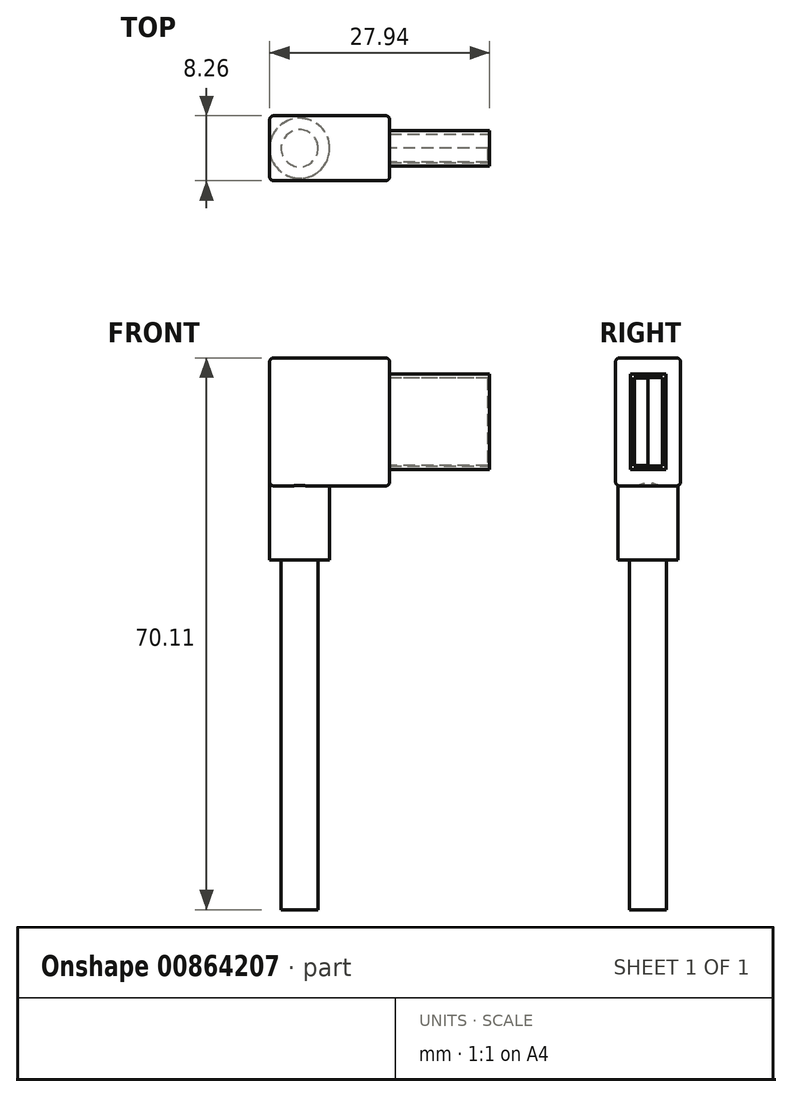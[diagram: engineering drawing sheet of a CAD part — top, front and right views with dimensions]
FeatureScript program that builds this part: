
annotation { "Feature Type Name" : "Feature", "Feature Type Description" : "" }
export const myFeature = defineFeature(function(context is Context, id is Id, definition is map)
    precondition{}
    {
        {
            var Q0;
            Q0=qCreatedBy(makeId("Front.planeOp"),FACE);
            var sketch = newSketch(context, id + "F0", { "sketchPlane" : qUnion([Q0])});
            skLineSegment(sketch, "E0.bottom", {"start": v(6.35, -6.08) * mm, "end": v(-6.35, -6.08) * mm});
            skLineSegment(sketch, "E0.top", {"start": v(6.35, 6.08) * mm, "end": v(-6.35, 6.08) * mm});
            skLineSegment(sketch, "E0.left", {"start": v(6.35, -6.08) * mm, "end": v(6.35, 6.08) * mm});
            skLineSegment(sketch, "E0.right", {"start": v(-6.35, -6.08) * mm, "end": v(-6.35, 6.08) * mm});
            skPoint(sketch, "E0.middle", {"position": v(0, 0) * mm});
            skLineSegment(sketch, "E1.bottom", {"start": v(-21.59, -8.13) * mm, "end": v(-6.35, -8.13) * mm});
            skLineSegment(sketch, "E1.top", {"start": v(-21.59, 8.13) * mm, "end": v(-6.35, 8.13) * mm});
            skLineSegment(sketch, "E1.left", {"start": v(-21.59, -8.13) * mm, "end": v(-21.59, 8.13) * mm});
            skLineSegment(sketch, "E1.right", {"start": v(-6.35, -8.13) * mm, "end": v(-6.35, 8.13) * mm});
            skPoint(sketch, "E1.middle", {"position": v(-13.97, 0) * mm});
            skSolve(sketch);
        }
        {
            var Q0;
            {var subQ0=sQuery(id+"F0.wireOp",EDGE,"E0.bottom");Q0=makeQuery(id+"F0.imprint","IMPRINT",FACE,{"disambiguationData":[TD([[makeQuery(id+"F0.imprint","IMPRINT",EDGE,{"derivedFrom":subQ0}),-1.0]])]});}
            extrude(context, id + "F1", {"entities" : qUnion([Q0]), "endBound" : BoundingType.SYMMETRIC, "depth" : 4.52 * mm, "offsetDistance" : 25.4 * mm});
        }
        {
            var Q0;
            {var subQ2=sQuery(id+"F0.wireOp",EDGE,"E1.bottom");Q0=makeQuery(id+"F0.imprint","IMPRINT",FACE,{"disambiguationData":[TD([[makeQuery(id+"F0.imprint","IMPRINT",EDGE,{"derivedFrom":subQ2}),1.0]])]});}
            extrude(context, id + "F2", {"entities" : qUnion([Q0]), "operationType" : NewBodyOperationType.ADD, "endBound" : BoundingType.SYMMETRIC, "depth" : 8.25 * mm, "offsetDistance" : 25.4 * mm});
        }
        {
            var Q0;
            Q0=makeQuery(id+"F1.opExtrude","SWEPT_FACE",FACE,{"disambiguationData":[OSD([sQuery(id+"F0.wireOp",EDGE,"E0.left")])]});
            var sketch = newSketch(context, id + "F3", { "sketchPlane" : qUnion([Q0])});
            skLineSegment(sketch, "E2.0", {"start": v(1.8, -5.62) * mm, "end": v(1.8, 5.62) * mm});
            skLineSegment(sketch, "E2.1", {"start": v(-1.8, -5.62) * mm, "end": v(1.8, -5.62) * mm});
            skLineSegment(sketch, "E2.2", {"start": v(-1.8, 5.62) * mm, "end": v(-1.8, -5.62) * mm});
            skLineSegment(sketch, "E2.3", {"start": v(1.8, 5.62) * mm, "end": v(-1.8, 5.62) * mm});
            skSolve(sketch);
        }
        {
            var Q0;
            Q0 = qSketchRegion(id + "F3", true);
            extrude(context, id + "F4", {"entities" : qUnion([Q0]), "operationType" : NewBodyOperationType.REMOVE, "oppositeDirection" : true, "depth" : 12.7 * mm, "offsetDistance" : 25.4 * mm});
        }
        {
            var Q0;
            Q0 = qSketchRegion(id + "F3", true);
            extrude(context, id + "F5", {"entities" : qUnion([Q0]), "operationType" : NewBodyOperationType.REMOVE, "oppositeDirection" : true, "depth" : 12.7 * mm, "offsetDistance" : 25.4 * mm});
        }
        {
            var Q0;
            Q0=makeQuery(id+"F2.opExtrude","CAP_FACE",FACE,{"disambiguationData":[OSD([sQuery(id+"F0.wireOp",EDGE,"E1.bottom"),sQuery(id+"F0.wireOp",EDGE,"E1.top"),sQuery(id+"F0.wireOp",EDGE,"E1.left"),sQuery(id+"F0.wireOp",EDGE,"E1.right")])],"isStart":false});
            var Q1;
            Q1=makeQuery(id+"F2.opExtrude","CAP_FACE",FACE,{"disambiguationData":[OSD([sQuery(id+"F0.wireOp",EDGE,"E1.bottom"),sQuery(id+"F0.wireOp",EDGE,"E1.top"),sQuery(id+"F0.wireOp",EDGE,"E1.left"),sQuery(id+"F0.wireOp",EDGE,"E1.right")])],"isStart":true});
            var Q2;
            Q2=makeQuery(id+"F2.opExtrude","SWEPT_FACE",FACE,{"disambiguationData":[OSD([sQuery(id+"F0.wireOp",EDGE,"E1.left")])]});
            var Q3;
            Q3=makeQuery(id+"F2.opExtrude","SWEPT_EDGE",EDGE,{"disambiguationData":[OSD([sQuery(id+"F0.wireOp",EDGE,"E1.top"),sQuery(id+"F0.wireOp",EDGE,"E1.right")])]});
            var Q4;
            Q4=makeQuery(id+"F2.opExtrude","SWEPT_EDGE",EDGE,{"disambiguationData":[OSD([sQuery(id+"F0.wireOp",EDGE,"E1.bottom"),sQuery(id+"F0.wireOp",EDGE,"E1.right")])]});
            fillet(context, id + "F6", {"entities" : qUnion([Q0, Q1, Q2, Q3, Q4]), "radius" : 0.5 * mm, "tangentPropagation" : true, "allowEdgeOverflow" : false});
        }
        {
            var Q0;
            Q0=makeQuery(id+"F4.boolean.opBoolean","COPY",FACE,{"derivedFrom":makeQuery(id+"F4.opExtrude","CAP_FACE",FACE,{"disambiguationData":[OSD([sQuery(id+"F3.wireOp",EDGE,"E2.0"),sQuery(id+"F3.wireOp",EDGE,"E2.1"),sQuery(id+"F3.wireOp",EDGE,"E2.2"),sQuery(id+"F3.wireOp",EDGE,"E2.3")])],"isStart":false})});
            var sketch = newSketch(context, id + "F7", { "sketchPlane" : qUnion([Q0])});
            skLineSegment(sketch, "E3.0", {"start": v(1.75, -5.57) * mm, "end": v(1.75, 5.57) * mm});
            skLineSegment(sketch, "E3.1", {"start": v(-1.75, -5.57) * mm, "end": v(1.75, -5.57) * mm});
            skLineSegment(sketch, "E3.2", {"start": v(-1.75, 5.57) * mm, "end": v(-1.75, -5.57) * mm});
            skLineSegment(sketch, "E3.3", {"start": v(1.75, 5.57) * mm, "end": v(-1.75, 5.57) * mm});
            skLineSegment(sketch, "E4", {"start": v(0, 5.62) * mm, "end": v(0, -5.57) * mm});
            skSolve(sketch);
        }
        {
            var Q0;
            {var subQ0=sQuery(id+"F7.wireOp",EDGE,"E3.2");Q0=makeQuery(id+"F7.imprint","IMPRINT",FACE,{"disambiguationData":[TD([[makeQuery(id+"F7.imprint","IMPRINT",EDGE,{"derivedFrom":subQ0}),1.0]])]});}
            extrude(context, id + "F8", {"entities" : qUnion([Q0]), "operationType" : NewBodyOperationType.ADD, "depth" : 12.45 * mm, "offsetDistance" : 25.4 * mm});
        }
        {
            var Q0;
            Q0=makeQuery(id+"F2.opExtrude","SWEPT_FACE",FACE,{"disambiguationData":[OSD([sQuery(id+"F0.wireOp",EDGE,"E1.bottom")])]});
            var sketch = newSketch(context, id + "F9", { "sketchPlane" : qUnion([Q0])});
            skLineSegment(sketch, "E5.0", {"start": v(-21.59, -3.62) * mm, "end": v(-21.59, 3.62) * mm});
            skLineSegment(sketch, "E6", {"start": v(-21.59, 0) * mm, "end": v(-13.97, 0) * mm});
            skCircle(sketch, "E7", {"center": v(-17.78, 0) * mm, "radius": 3.8 * mm});
            skSolve(sketch);
        }
        {
            var Q0;
            Q0 = qSketchRegion(id + "F9", true);
            extrude(context, id + "F10", {"entities" : qUnion([Q0]), "operationType" : NewBodyOperationType.ADD, "depth" : 9.4 * mm, "offsetDistance" : 25.4 * mm, "hasSecondDirection" : true, "secondDirectionOppositeDirection" : true, "secondDirectionDepth" : 0.5 * mm});
        }
        {
            var Q0;
            Q0=makeQuery(id+"F10.opExtrude","CAP_FACE",FACE,{"disambiguationData":[OSD([sQuery(id+"F9.wireOp",EDGE,"E7")])],"isStart":false});
            var sketch = newSketch(context, id + "F11", { "sketchPlane" : qUnion([Q0])});
            skCircle(sketch, "E8", {"center": v(-17.78, 0) * mm, "radius": 2.35 * mm});
            skSolve(sketch);
        }
        {
            var Q0;
            Q0 = qSketchRegion(id + "F11", true);
            extrude(context, id + "F12", {"entities" : qUnion([Q0]), "operationType" : NewBodyOperationType.ADD, "depth" : 44.45 * mm, "offsetDistance" : 25.4 * mm});
        }
    });
